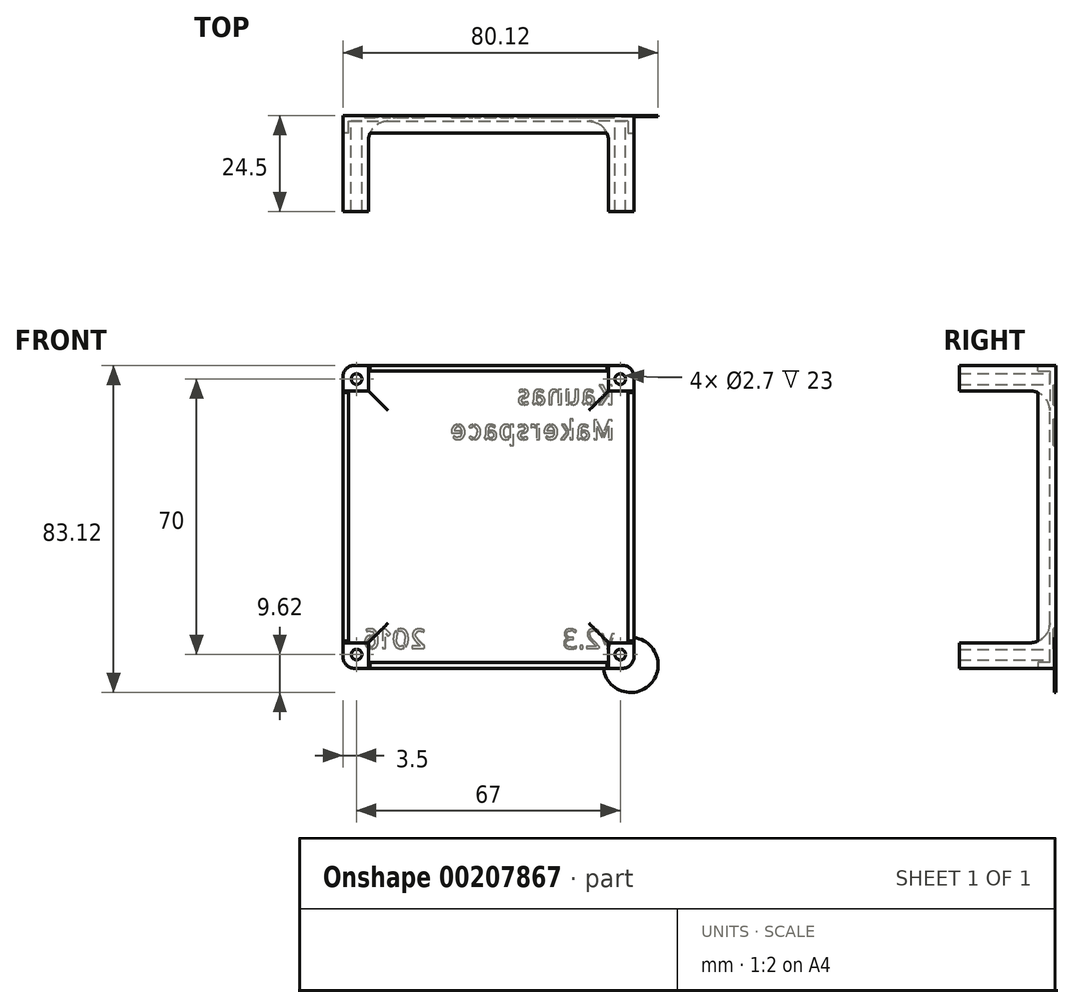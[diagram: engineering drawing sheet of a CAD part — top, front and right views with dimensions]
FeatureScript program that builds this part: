
annotation { "Feature Type Name" : "Feature", "Feature Type Description" : "" }
export const myFeature = defineFeature(function(context is Context, id is Id, definition is map)
    precondition{}
    {
        {
            var Q0;
            Q0=qCreatedBy(makeId("Front.planeOp"),FACE);
            var sketch = newSketch(context, id + "F0", { "sketchPlane" : qUnion([Q0])});
            skLineSegment(sketch, "E0.bottom", {"start": v(0, 0) * mm, "end": v(74, 0) * mm});
            skLineSegment(sketch, "E0.top", {"start": v(0, -77) * mm, "end": v(74, -77) * mm});
            skLineSegment(sketch, "E0.left", {"start": v(0, 0) * mm, "end": v(0, -77) * mm});
            skLineSegment(sketch, "E0.right", {"start": v(74, 0) * mm, "end": v(74, -77) * mm});
            skLineSegment(sketch, "E1.bottom", {"start": v(72.5, -1.5) * mm, "end": v(1.5, -1.5) * mm});
            skLineSegment(sketch, "E1.top", {"start": v(72.5, -75.5) * mm, "end": v(1.5, -75.5) * mm});
            skLineSegment(sketch, "E1.left", {"start": v(72.5, -1.5) * mm, "end": v(72.5, -75.5) * mm});
            skLineSegment(sketch, "E1.right", {"start": v(1.5, -1.5) * mm, "end": v(1.5, -75.5) * mm});
            skLineSegment(sketch, "E2", {"start": v(37, -1.5) * mm, "end": v(37, 0) * mm, "construction": true});
            skLineSegment(sketch, "E3", {"start": v(72.5, -38.5) * mm, "end": v(74, -38.5) * mm, "construction": true});
            skSolve(sketch);
        }
        {
            var Q0;
            Q0 = qSketchRegion(id + "F0", true);
            var Q1;
            Q1=makeQuery(id+"F0.imprint","IMPRINT",FACE,{"disambiguationData":[TD([[makeQuery(id+"F0.imprint","IMPRINT",EDGE,{"derivedFrom":sQuery(id+"F0.wireOp",EDGE,"E1.bottom")}),1.0]])]});
            extrude(context, id + "F1", {"entities" : qUnion([Q0, Q1]), "depth" : 1.5 * mm});
        }
        {
            var Q0;
            Q0=makeQuery(id+"F0.imprint","IMPRINT",FACE,{"disambiguationData":[TD([[makeQuery(id+"F0.imprint","IMPRINT",EDGE,{"derivedFrom":sQuery(id+"F0.wireOp",EDGE,"E0.bottom")}),-1.0]])]});
            extrude(context, id + "F2", {"entities" : qUnion([Q0]), "operationType" : NewBodyOperationType.ADD, "depth" : 4.5 * mm});
        }
        {
            var Q0;
            Q0=makeQuery(id+"F1.opExtrude","CAP_FACE",FACE,{"disambiguationData":[OSD([sQuery(id+"F0.wireOp",EDGE,"E0.bottom"),sQuery(id+"F0.wireOp",EDGE,"E0.top"),sQuery(id+"F0.wireOp",EDGE,"E0.left"),sQuery(id+"F0.wireOp",EDGE,"E0.right")])],"isStart":false});
            var sketch = newSketch(context, id + "F3", { "sketchPlane" : qUnion([Q0])});
            skLineSegment(sketch, "E4.bottom", {"start": v(3.5, -3.5) * mm, "end": v(70.5, -3.5) * mm, "construction": true});
            skLineSegment(sketch, "E4.top", {"start": v(3.5, -73.5) * mm, "end": v(70.5, -73.5) * mm, "construction": true});
            skLineSegment(sketch, "E4.left", {"start": v(3.5, -3.5) * mm, "end": v(3.5, -73.5) * mm, "construction": true});
            skLineSegment(sketch, "E4.right", {"start": v(70.5, -3.5) * mm, "end": v(70.5, -73.5) * mm, "construction": true});
            skLineSegment(sketch, "E5", {"start": v(37, -3.5) * mm, "end": v(37, 0) * mm, "construction": true});
            skLineSegment(sketch, "E6", {"start": v(3.5, -38.5) * mm, "end": v(0, -38.5) * mm, "construction": true});
            skCircle(sketch, "E7", {"center": v(3.5, -3.5) * mm, "radius": 1.35 * mm});
            skCircle(sketch, "E8", {"center": v(70.5, -3.5) * mm, "radius": 1.35 * mm});
            skCircle(sketch, "E9", {"center": v(70.5, -73.5) * mm, "radius": 1.35 * mm});
            skCircle(sketch, "E10", {"center": v(3.5, -73.5) * mm, "radius": 1.35 * mm});
            skLineSegment(sketch, "E11.bottom", {"start": v(6.5, -6.5) * mm, "end": v(67.5, -6.5) * mm, "construction": true});
            skLineSegment(sketch, "E11.top", {"start": v(6.5, -70.5) * mm, "end": v(67.5, -70.5) * mm, "construction": true});
            skLineSegment(sketch, "E11.left", {"start": v(6.5, -6.5) * mm, "end": v(6.5, -70.5) * mm, "construction": true});
            skLineSegment(sketch, "E11.right", {"start": v(67.5, -6.5) * mm, "end": v(67.5, -70.5) * mm, "construction": true});
            skLineSegment(sketch, "E12", {"start": v(37, -6.5) * mm, "end": v(37, -3.5) * mm, "construction": true});
            skLineSegment(sketch, "E13", {"start": v(6.5, -38.5) * mm, "end": v(3.5, -38.5) * mm, "construction": true});
            skLineSegment(sketch, "E14.bottom", {"start": v(0, 0) * mm, "end": v(6.5, 0) * mm});
            skLineSegment(sketch, "E14.top", {"start": v(0, -6.5) * mm, "end": v(6.5, -6.5) * mm});
            skLineSegment(sketch, "E14.left", {"start": v(0, 0) * mm, "end": v(0, -6.5) * mm});
            skLineSegment(sketch, "E14.right", {"start": v(6.5, 0) * mm, "end": v(6.5, -6.5) * mm});
            skLineSegment(sketch, "E15.bottom", {"start": v(74, 0) * mm, "end": v(67.5, 0) * mm});
            skLineSegment(sketch, "E15.top", {"start": v(74, -6.5) * mm, "end": v(67.5, -6.5) * mm});
            skLineSegment(sketch, "E15.left", {"start": v(74, 0) * mm, "end": v(74, -6.5) * mm});
            skLineSegment(sketch, "E15.right", {"start": v(67.5, 0) * mm, "end": v(67.5, -6.5) * mm});
            skLineSegment(sketch, "E16.bottom", {"start": v(74, -77) * mm, "end": v(67.5, -77) * mm});
            skLineSegment(sketch, "E16.top", {"start": v(74, -70.5) * mm, "end": v(67.5, -70.5) * mm});
            skLineSegment(sketch, "E16.left", {"start": v(74, -77) * mm, "end": v(74, -70.5) * mm});
            skLineSegment(sketch, "E16.right", {"start": v(67.5, -77) * mm, "end": v(67.5, -70.5) * mm});
            skLineSegment(sketch, "E17.bottom", {"start": v(0, -77) * mm, "end": v(6.5, -77) * mm});
            skLineSegment(sketch, "E17.top", {"start": v(0, -70.5) * mm, "end": v(6.5, -70.5) * mm});
            skLineSegment(sketch, "E17.left", {"start": v(0, -77) * mm, "end": v(0, -70.5) * mm});
            skLineSegment(sketch, "E17.right", {"start": v(6.5, -77) * mm, "end": v(6.5, -70.5) * mm});
            skSolve(sketch);
        }
        {
            var Q0;
            Q0 = qSketchRegion(id + "F3", true);
            extrude(context, id + "F4", {"entities" : qUnion([Q0]), "operationType" : NewBodyOperationType.ADD, "depth" : (30.1 - 4 - 1.5 - 1.6) * mm});
        }
        {
            var Q0;
            Q0=makeQuery(id+"F4.opExtrude","CAP_EDGE",EDGE,{"disambiguationData":[OSD([sQuery(id+"F3.wireOp",EDGE,"E14.top")])],"isStart":true});
            var Q1;
            Q1=makeQuery(id+"F4.opExtrude","CAP_EDGE",EDGE,{"disambiguationData":[OSD([sQuery(id+"F3.wireOp",EDGE,"E17.right")])],"isStart":true});
            var Q2;
            Q2=makeQuery(id+"F4.opExtrude","CAP_EDGE",EDGE,{"disambiguationData":[OSD([sQuery(id+"F3.wireOp",EDGE,"E17.top")])],"isStart":true});
            var Q3;
            Q3=makeQuery(id+"F4.opExtrude","CAP_EDGE",EDGE,{"disambiguationData":[OSD([sQuery(id+"F3.wireOp",EDGE,"E16.top")])],"isStart":true});
            var Q4;
            Q4=makeQuery(id+"F4.opExtrude","CAP_EDGE",EDGE,{"disambiguationData":[OSD([sQuery(id+"F3.wireOp",EDGE,"E16.right")])],"isStart":true});
            var Q5;
            Q5=makeQuery(id+"F4.opExtrude","CAP_EDGE",EDGE,{"disambiguationData":[OSD([sQuery(id+"F3.wireOp",EDGE,"E15.right")])],"isStart":true});
            var Q6;
            Q6=makeQuery(id+"F4.opExtrude","CAP_EDGE",EDGE,{"disambiguationData":[OSD([sQuery(id+"F3.wireOp",EDGE,"E15.top")])],"isStart":true});
            var Q7;
            Q7=makeQuery(id+"F4.opExtrude","CAP_EDGE",EDGE,{"disambiguationData":[OSD([sQuery(id+"F3.wireOp",EDGE,"E14.right")])],"isStart":true});
            fillet(context, id + "F5", {"entities" : qUnion([Q0, Q1, Q2, Q3, Q4, Q5, Q6, Q7]), "radius" : 5 * mm, "tangentPropagation" : true, "allowEdgeOverflow" : false});
        }
        {
            var Q0;
            Q0=makeQuery(id+"F1.opExtrude","CAP_FACE",FACE,{"disambiguationData":[OSD([sQuery(id+"F0.wireOp",EDGE,"E0.bottom"),sQuery(id+"F0.wireOp",EDGE,"E0.top"),sQuery(id+"F0.wireOp",EDGE,"E0.left"),sQuery(id+"F0.wireOp",EDGE,"E0.right")])],"isStart":true});
            var sketch = newSketch(context, id + "F6", { "sketchPlane" : qUnion([Q0])});
            skText(sketch, "E18", { "text": "Kaunas\nMakerspace", "fontName": "AllertaStencil-Regular.ttf"});
            skText(sketch, "E19", { "text": "2016", "fontName": "AllertaStencil-Regular.ttf"});
            skText(sketch, "E20", { "text": "v2.3", "fontName": "OpenSans-Regular.ttf"});
            skLineSegment(sketch, "E21.bottom", {"start": v(-69, -5) * mm, "end": v(-5, -5) * mm, "construction": true});
            skLineSegment(sketch, "E21.top", {"start": v(-69, -72) * mm, "end": v(-5, -72) * mm, "construction": true});
            skLineSegment(sketch, "E21.left", {"start": v(-69, -5) * mm, "end": v(-69, -72) * mm, "construction": true});
            skLineSegment(sketch, "E21.right", {"start": v(-5, -5) * mm, "end": v(-5, -72) * mm, "construction": true});
            skLineSegment(sketch, "E22", {"start": v(-69, -38.5) * mm, "end": v(-74, -38.5) * mm, "construction": true});
            skLineSegment(sketch, "E23", {"start": v(-37, -5) * mm, "end": v(-37, 0) * mm, "construction": true});
            const initialGuessF6  = {"E18": [-0.069, -0.01, 1, 0, 0.005], "E19": [-0.02132, -0.072, 1, 0, 0.005], "E20": [-0.069, -0.072, 1, 0, 0.005]};
            skSetInitialGuess(sketch, initialGuessF6);
            skSolve(sketch);
        }
        {
            var Q0;
            Q0 = qSketchRegion(id + "F6", true);
            extrude(context, id + "F7", {"entities" : qUnion([Q0]), "operationType" : NewBodyOperationType.REMOVE, "oppositeDirection" : true, "depth" : 0.6 * mm});
        }
        {
            var Q0;
            Q0=makeQuery(id+"F4.boolean.opBoolean","MERGE",EDGE,{"derivedFrom":[makeQuery(id+"F1.opExtrude","SWEPT_EDGE",EDGE,{"disambiguationData":[OSD([sQuery(id+"F0.wireOp",EDGE,"E0.top"),sQuery(id+"F0.wireOp",EDGE,"E0.left")])]}),makeQuery(id+"F4.opExtrude","SWEPT_EDGE",EDGE,{"disambiguationData":[OSD([sQuery(id+"F3.wireOp",EDGE,"E17.bottom"),sQuery(id+"F3.wireOp",EDGE,"E17.left")])]})]});
            var Q1;
            Q1=makeQuery(id+"F4.boolean.opBoolean","MERGE",EDGE,{"derivedFrom":[makeQuery(id+"F1.opExtrude","SWEPT_EDGE",EDGE,{"disambiguationData":[OSD([sQuery(id+"F0.wireOp",EDGE,"E0.top"),sQuery(id+"F0.wireOp",EDGE,"E0.right")])]}),makeQuery(id+"F4.opExtrude","SWEPT_EDGE",EDGE,{"disambiguationData":[OSD([sQuery(id+"F3.wireOp",EDGE,"E16.bottom"),sQuery(id+"F3.wireOp",EDGE,"E16.left")])]})]});
            var Q2;
            Q2=makeQuery(id+"F4.boolean.opBoolean","MERGE",EDGE,{"derivedFrom":[makeQuery(id+"F1.opExtrude","SWEPT_EDGE",EDGE,{"disambiguationData":[OSD([sQuery(id+"F0.wireOp",EDGE,"E0.bottom"),sQuery(id+"F0.wireOp",EDGE,"E0.right")])]}),makeQuery(id+"F4.opExtrude","SWEPT_EDGE",EDGE,{"disambiguationData":[OSD([sQuery(id+"F3.wireOp",EDGE,"E15.bottom"),sQuery(id+"F3.wireOp",EDGE,"E15.left")])]})]});
            var Q3;
            Q3=makeQuery(id+"F4.boolean.opBoolean","MERGE",EDGE,{"derivedFrom":[makeQuery(id+"F1.opExtrude","SWEPT_EDGE",EDGE,{"disambiguationData":[OSD([sQuery(id+"F0.wireOp",EDGE,"E0.bottom"),sQuery(id+"F0.wireOp",EDGE,"E0.left")])]}),makeQuery(id+"F4.opExtrude","SWEPT_EDGE",EDGE,{"disambiguationData":[OSD([sQuery(id+"F3.wireOp",EDGE,"E14.bottom"),sQuery(id+"F3.wireOp",EDGE,"E14.left")])]})]});
            fillet(context, id + "F8", {"entities" : qUnion([Q0, Q1, Q2, Q3]), "radius" : 3 * mm, "tangentPropagation" : true, "allowEdgeOverflow" : false});
        }
        {
            var Q0;
            Q0=makeQuery(id+"F1.opExtrude","CAP_FACE",FACE,{"disambiguationData":[OSD([sQuery(id+"F0.wireOp",EDGE,"E0.bottom"),sQuery(id+"F0.wireOp",EDGE,"E0.top"),sQuery(id+"F0.wireOp",EDGE,"E0.left"),sQuery(id+"F0.wireOp",EDGE,"E0.right")])],"isStart":true});
            var sketch = newSketch(context, id + "F9", { "sketchPlane" : qUnion([Q0])});
            skArc(sketch, "E24", {"start": v(-7.82, 0) * mm, "mid": v(4.07, 4.07) * mm, "end": v(0, -7.82) * mm});
            skArc(sketch, "E25", {"start": v(0, -69.18) * mm, "mid": v(4.07, -81.07) * mm, "end": v(-7.82, -77) * mm});
            skArc(sketch, "E26", {"start": v(-74, -7.82) * mm, "mid": v(-78.07, 4.07) * mm, "end": v(-66.18, 0) * mm});
            skArc(sketch, "E27", {"start": v(-74, -69.18) * mm, "mid": v(-78.07, -81.07) * mm, "end": v(-66.18, -77) * mm});
            skSolve(sketch);
        }
        {
            var Q0;
            {var subQ0=sQuery(id+"F9.wireOp",EDGE,"E26");Q0=makeQuery(id+"F9.imprint","IMPRINT",FACE,{"disambiguationData":[TD([[makeQuery(id+"F9.imprint","IMPRINT",EDGE,{"derivedFrom":subQ0}),-1.0]])]});}
            var Q1;
            {var subQ0=sQuery(id+"F9.wireOp",EDGE,"E24");Q1=makeQuery(id+"F9.imprint","IMPRINT",FACE,{"disambiguationData":[TD([[makeQuery(id+"F9.imprint","IMPRINT",EDGE,{"derivedFrom":subQ0}),-1.0]])]});}
            var Q2;
            {var subQ0=sQuery(id+"F9.wireOp",EDGE,"E25");Q2=makeQuery(id+"F9.imprint","IMPRINT",FACE,{"disambiguationData":[TD([[makeQuery(id+"F9.imprint","IMPRINT",EDGE,{"derivedFrom":subQ0}),-1.0]])]});}
            var Q3;
            {var subQ0=sQuery(id+"F9.wireOp",EDGE,"E27");Q3=makeQuery(id+"F9.imprint","IMPRINT",FACE,{"disambiguationData":[TD([[makeQuery(id+"F9.imprint","IMPRINT",EDGE,{"derivedFrom":subQ0}),1.0]])]});}
            extrude(context, id + "F10", {"entities" : qUnion([Q0, Q1, Q2, Q3]), "operationType" : NewBodyOperationType.ADD, "oppositeDirection" : true, "depth" : 0.3 * mm});
        }
    });
